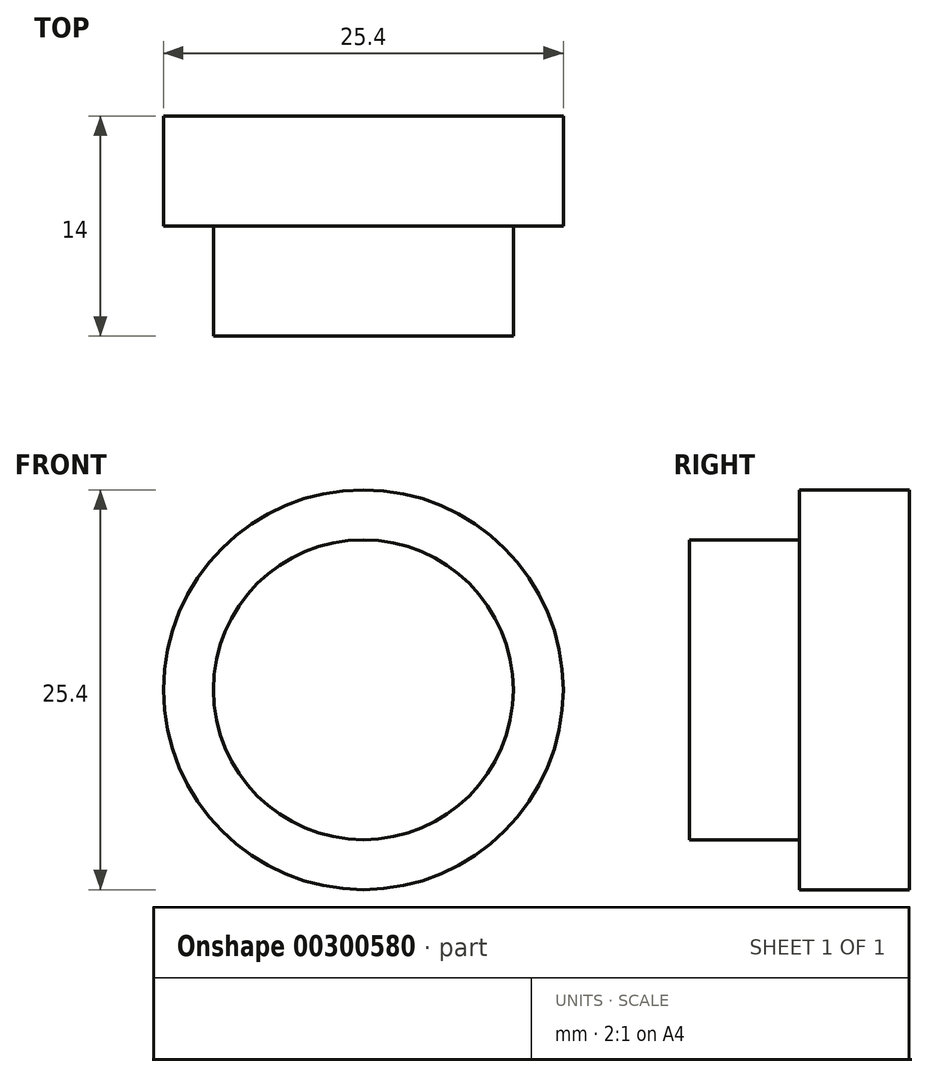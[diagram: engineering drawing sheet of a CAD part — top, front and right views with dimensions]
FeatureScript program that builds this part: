
annotation { "Feature Type Name" : "Feature", "Feature Type Description" : "" }
export const myFeature = defineFeature(function(context is Context, id is Id, definition is map)
    precondition{}
    {
        {
            var Q0;
            Q0=qCreatedBy(makeId("Front.planeOp"),FACE);
            var sketch = newSketch(context, id + "F0", { "sketchPlane" : qUnion([Q0])});
            skCircle(sketch, "E0", {"center": v(0, 0) * mm, "radius": 9.53 * mm});
            skSolve(sketch);
        }
        {
            var Q0;
            Q0=makeQuery(id+"F0.imprint","IMPRINT",FACE,{"disambiguationData":[TD([[makeQuery(id+"F0.imprint","IMPRINT",EDGE,{"derivedFrom":sQuery(id+"F0.wireOp",EDGE,"E0")}),1.0]])]});
            var Q1;
            Q1=sQuery(id+"F0.wireOp",EDGE,"E0");
            extrude(context, id + "F1", {"entities" : qUnion([Q0]), "surfaceEntities" : qUnion([Q1]), "depth" : 7 * mm, "offsetDistance" : 25.4 * mm});
        }
        {
            var Q0;
            Q0=makeQuery(id+"F1.opExtrude","CAP_FACE",FACE,{"disambiguationData":[OSD([sQuery(id+"F0.wireOp",EDGE,"E0")])],"isStart":true});
            var sketch = newSketch(context, id + "F2", { "sketchPlane" : qUnion([Q0])});
            skCircle(sketch, "E1", {"center": v(0, 0) * mm, "radius": 12.7 * mm});
            skSolve(sketch);
        }
        {
            var Q0;
            Q0 = qSketchRegion(id + "F2", true);
            extrude(context, id + "F3", {"entities" : qUnion([Q0]), "operationType" : NewBodyOperationType.ADD, "depth" : 7 * mm, "offsetDistance" : 25.4 * mm});
        }
    });
